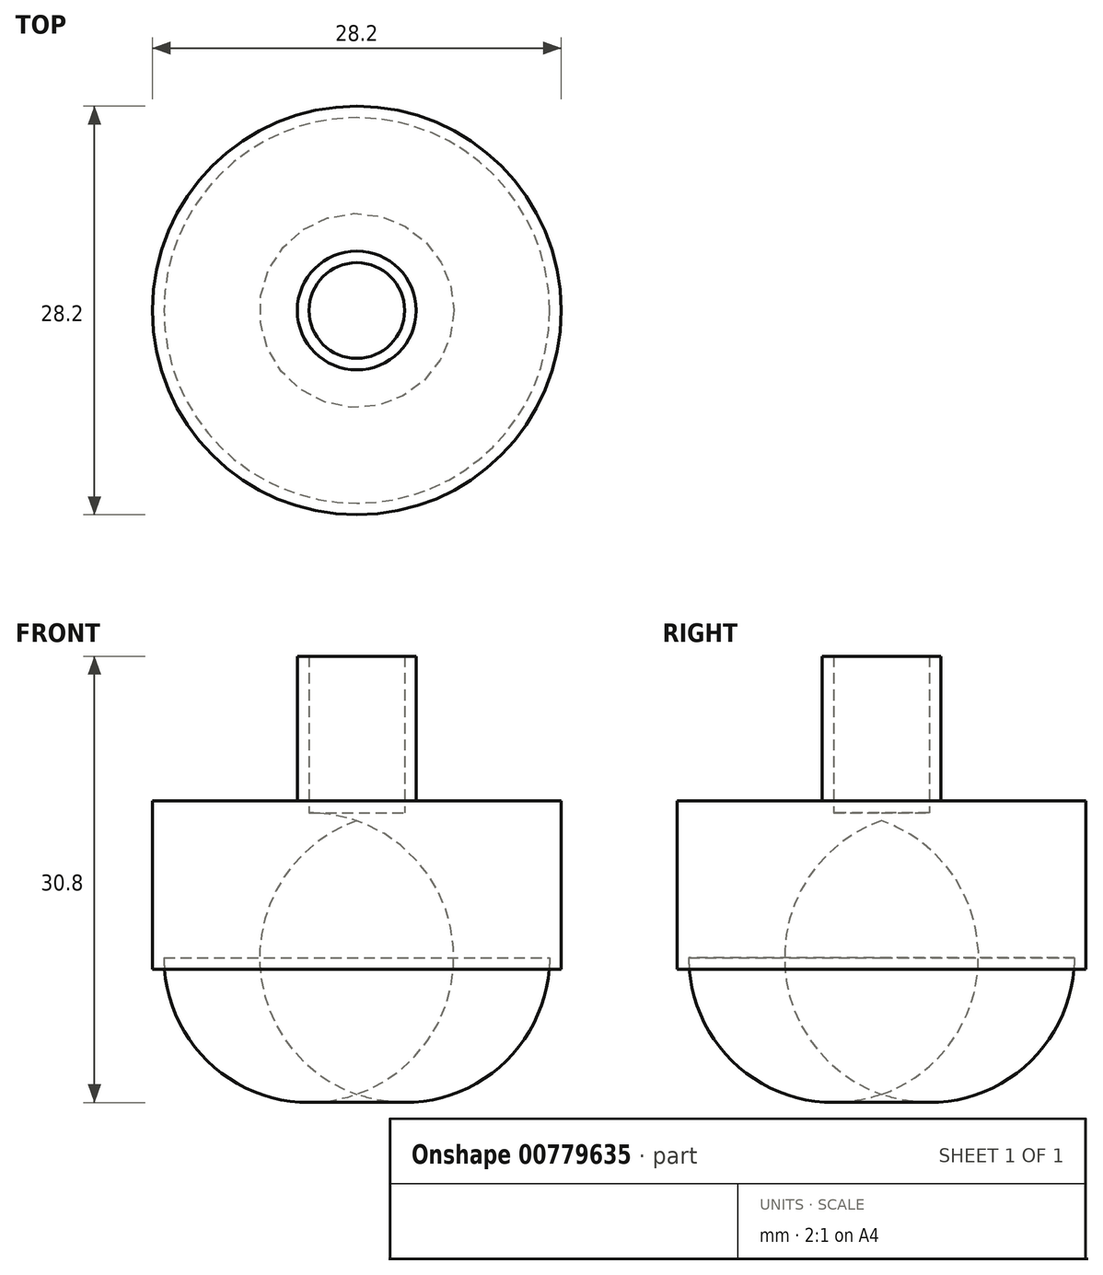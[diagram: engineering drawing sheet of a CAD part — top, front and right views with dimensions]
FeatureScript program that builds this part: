
annotation { "Feature Type Name" : "Feature", "Feature Type Description" : "" }
export const myFeature = defineFeature(function(context is Context, id is Id, definition is map)
    precondition{}
    {
        {
            var Q0;
            Q0=qCreatedBy(makeId("Front.planeOp"),FACE);
            var sketch = newSketch(context, id + "F0", { "sketchPlane" : qUnion([Q0])});
            skLineSegment(sketch, "E0", {"start": v(0, -2.42) * mm, "end": v(0, 2.58) * mm, "construction": true});
            skLineSegment(sketch, "E1", {"start": v(0, 2.58) * mm, "end": v(0, 7.58) * mm, "construction": true});
            skLineSegment(sketch, "E2", {"start": v(0, -2.42) * mm, "end": v(13.3, -2.42) * mm});
            skLineSegment(sketch, "E3", {"start": v(13.3, -2.42) * mm, "end": v(13.3, 2.58) * mm});
            skLineSegment(sketch, "E4", {"start": v(3.3, 7.58) * mm, "end": v(0, 7.58) * mm, "construction": true});
            skPoint(sketch, "E5.visualSharp", {"position": v(13.3, 7.58) * mm});
            skArc(sketch, "E5.filletArc", {"start": v(13.3, -2.42) * mm, "mid": v(10.37, 4.65) * mm, "end": v(3.3, 7.58) * mm});
            skLineSegment(sketch, "E6", {"start": v(0, -2.42) * mm, "end": v(0, -3.22) * mm});
            skLineSegment(sketch, "E7", {"start": v(0, -3.22) * mm, "end": v(14.1, -3.22) * mm});
            skLineSegment(sketch, "E8", {"start": v(14.1, -3.22) * mm, "end": v(14.1, 2.58) * mm});
            skLineSegment(sketch, "E9", {"start": v(14.1, 2.58) * mm, "end": v(14.1, 8.38) * mm});
            skLineSegment(sketch, "E10", {"start": v(13.3, -5.97) * mm, "end": v(14.1, -5.97) * mm, "construction": true});
            skLineSegment(sketch, "E11", {"start": v(8.47, -2.42) * mm, "end": v(8.47, -3.22) * mm, "construction": true});
            skLineSegment(sketch, "E12", {"start": v(3.3, 7.58) * mm, "end": v(3.3, 18.38) * mm});
            skLineSegment(sketch, "E13", {"start": v(0, 7.58) * mm, "end": v(0, 8.38) * mm, "construction": true});
            skLineSegment(sketch, "E14", {"start": v(0, 8.38) * mm, "end": v(3.3, 8.38) * mm, "construction": true});
            skLineSegment(sketch, "E15", {"start": v(3.3, 8.38) * mm, "end": v(4.1, 8.38) * mm, "construction": true});
            skLineSegment(sketch, "E16", {"start": v(4.1, 8.38) * mm, "end": v(14.1, 8.38) * mm});
            skLineSegment(sketch, "E17", {"start": v(4.1, 8.38) * mm, "end": v(4.1, 18.38) * mm});
            skLineSegment(sketch, "E18", {"start": v(4.1, 18.38) * mm, "end": v(3.3, 18.38) * mm});
            skSolve(sketch);
        }
        {
            var Q0;
            Q0 = qSketchRegion(id + "F0", true);
            var Q1;
            Q1=sQuery(id+"F0.wireOp",EDGE,"E1");
            revolve(context, id + "F1", {"surfaceOperationType" : NewSurfaceOperationType.NEW, "entities" : qUnion([Q0]), "axis" : qUnion([Q1]), "revolveType" : RevolveType.FULL});
        }
    });
